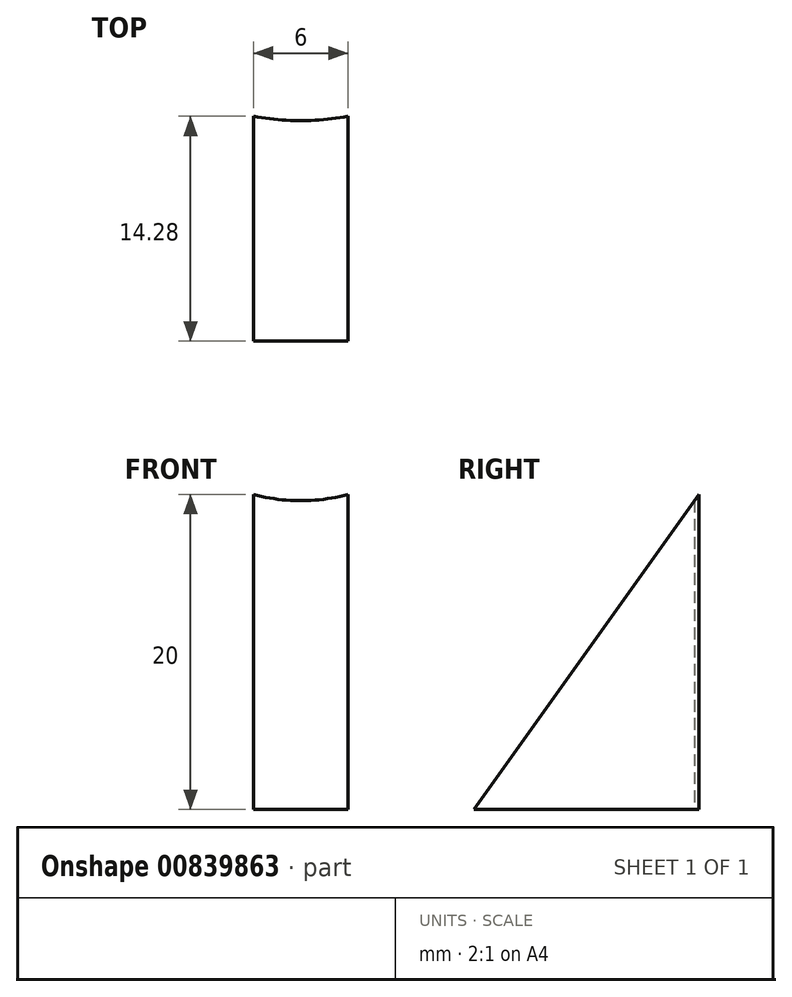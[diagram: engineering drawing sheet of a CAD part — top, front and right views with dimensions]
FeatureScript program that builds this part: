
annotation { "Feature Type Name" : "Feature", "Feature Type Description" : "" }
export const myFeature = defineFeature(function(context is Context, id is Id, definition is map)
    precondition{}
    {
        {
            var Q0;
            Q0=qCreatedBy(makeId("Top.planeOp"),FACE);
            var sketch = newSketch(context, id + "F0", { "sketchPlane" : qUnion([Q0])});
            skLineSegment(sketch, "E0.bottom", {"start": v(3, 7.14) * mm, "end": v(-3, 7.14) * mm});
            skLineSegment(sketch, "E0.top", {"start": v(3, -7.14) * mm, "end": v(-3, -7.14) * mm});
            skLineSegment(sketch, "E0.left", {"start": v(3, 7.14) * mm, "end": v(3, -7.14) * mm});
            skLineSegment(sketch, "E0.right", {"start": v(-3, 7.14) * mm, "end": v(-3, -7.14) * mm});
            skPoint(sketch, "E0.middle", {"position": v(0, 0) * mm});
            skSolve(sketch);
        }
        {
            var Q0;
            Q0=makeQuery(id+"F0.imprint","IMPRINT",FACE,{"disambiguationData":[TD([[makeQuery(id+"F0.imprint","IMPRINT",EDGE,{"derivedFrom":sQuery(id+"F0.wireOp",EDGE,"E0.bottom")}),1.0]])]});
            extrude(context, id + "F1", {"entities" : qUnion([Q0]), "depth" : 20 * mm, "offsetDistance" : 25 * mm});
        }
        {
            var Q0;
            Q0=makeQuery(id+"F1.opExtrude","CAP_EDGE",EDGE,{"disambiguationData":[OSD([sQuery(id+"F0.wireOp",EDGE,"E0.top")])],"isStart":false});
            chamfer(context, id + "F2", {"entities" : qUnion([Q0]), "chamferType" : ChamferType.TWO_OFFSETS, "width1" : 20 * mm, "oppositeDirection" : false, "width2" : 14.28 * mm, "tangentPropagation" : true});
        }
        {
            var Q0;
            Q0=qCreatedBy(makeId("Top.planeOp"),FACE);
            var sketch = newSketch(context, id + "F3", { "sketchPlane" : qUnion([Q0])});
            skPoint(sketch, "E1.0", {"position": v(3, 7.14) * mm});
            skPoint(sketch, "E2.0", {"position": v(-3, 7.14) * mm});
            skPoint(sketch, "E3", {"position": v(0, 22.86) * mm});
            skCircle(sketch, "E4", {"center": v(0, 22.86) * mm, "radius": 16 * mm});
            skSolve(sketch);
        }
        {
            var Q0;
            Q0=makeQuery(id+"F3.imprint","IMPRINT",FACE,{"disambiguationData":[TD([[makeQuery(id+"F3.imprint","IMPRINT",EDGE,{"derivedFrom":sQuery(id+"F3.wireOp",EDGE,"E4")}),1.0]])]});
            extrude(context, id + "F4", {"entities" : qUnion([Q0]), "operationType" : NewBodyOperationType.REMOVE, "depth" : 25 * mm, "offsetDistance" : 25 * mm});
        }
    });
